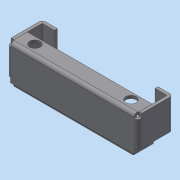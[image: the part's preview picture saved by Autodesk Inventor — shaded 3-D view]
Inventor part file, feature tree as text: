
AUTODESK INVENTOR PART (.ipt)
format: ipt  version: 2020 (Build 240168000, 168)  size: 258,048 bytes
history: native  units: mm
features: other x7, extrude x1
ambient origin geometry x8: Origin, YZ Plane, XZ Plane, XY Plane, X Axis, Y Axis, Z Axis, Center Point
bodies: Body1 (feature_tree)
feature tree (8):
  other  "實體1"
  extrude  "擠出1"  Depth=20.3mm
  other  "折彎零件4"
  other  "折彎零件5"
  other  "折彎零件3"
  other  "折彎零件6"
  other  "折彎零件1"
  other  "折彎零件2"
